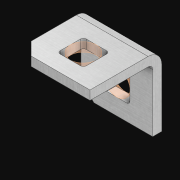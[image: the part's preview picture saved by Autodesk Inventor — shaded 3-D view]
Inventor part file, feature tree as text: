
AUTODESK INVENTOR PART (.ipt)
format: ipt  version: 2021 (Build 250183000, 183)  size: 522,240 bytes
history: native  units: in
note: dims shown in document units (in); Inventor stores cm internally (conversion verified against a paired STEP export)
features: extrude x3, sketch x3, other x2, pattern_linear x1, sheet_metal_op x1
ambient origin geometry x8: Origin, YZ Plane, XZ Plane, XY Plane, X Axis, Y Axis, Z Axis, Center Point
bodies: Solid1 (feature_tree)
feature tree (10):
  pattern_linear  "Rectangular Pattern1"  Spacing1=0.063in  [1 undecoded]
  extrude  "Extrusion1"  Depth=0.5in
  sketch  "Sketch1"  dims[d0=0.182in]
  other  "Srf1"
  sketch  "Sketch2"  dims[d1=0.063in d2=0.0in]
  other  "Srf2"
  sketch  "Sketch3"  dims[d3=0.182in d4=0.063in d5=0.0in d8=0.5in d9=17.0in d10=0.0in]
  sheet_metal_op  "Fold1"
  extrude  "ExtrusionSrf1"  Depth=0.5in TaperAngle=0.0deg
  extrude  "ExtrusionSrf2"  [1 undecoded]
note: 2 required parameter values undecoded (feature->parameter linkage not recoverable at this tier; creation-order binding heuristic only, values carry confidence <= 0.55)
